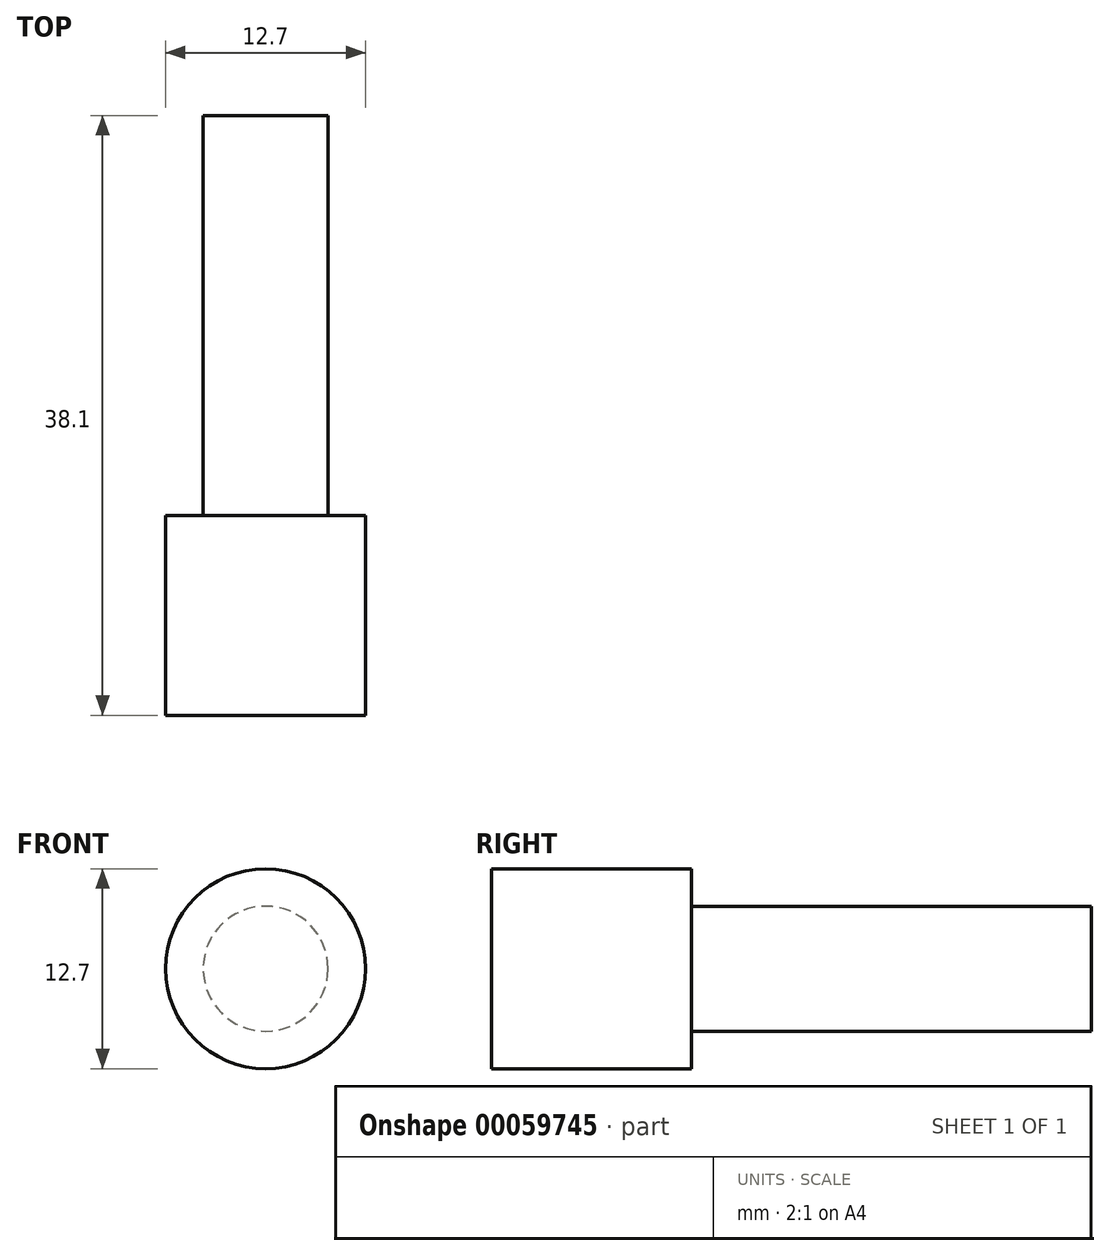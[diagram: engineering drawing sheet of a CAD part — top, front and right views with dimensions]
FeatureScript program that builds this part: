
annotation { "Feature Type Name" : "Feature", "Feature Type Description" : "" }
export const myFeature = defineFeature(function(context is Context, id is Id, definition is map)
    precondition{}
    {
        {
            var Q0;
            Q0=qCreatedBy(makeId("Front.planeOp"),FACE);
            var sketch = newSketch(context, id + "F0", { "sketchPlane" : qUnion([Q0])});
            skCircle(sketch, "E0", {"center": v(0, 0) * mm, "radius": 6.35 * mm});
            skSolve(sketch);
        }
        {
            var Q0;
            Q0=makeQuery(id+"F0.imprint","IMPRINT",FACE,{"disambiguationData":[TD([[makeQuery(id+"F0.imprint","IMPRINT",EDGE,{"derivedFrom":sQuery(id+"F0.wireOp",EDGE,"E0")}),1.0]])]});
            extrude(context, id + "F1", {"entities" : qUnion([Q0]), "depth" : 12.7 * mm});
        }
        {
            var Q0;
            Q0=makeQuery(id+"F1.opExtrude","CAP_FACE",FACE,{"disambiguationData":[OSD([sQuery(id+"F0.wireOp",EDGE,"E0")])],"isStart":true});
            var sketch = newSketch(context, id + "F2", { "sketchPlane" : qUnion([Q0])});
            skCircle(sketch, "E1", {"center": v(0, 0) * mm, "radius": 3.97 * mm});
            skSolve(sketch);
        }
        {
            var Q0;
            Q0=makeQuery(id+"F2.imprint","IMPRINT",FACE,{"disambiguationData":[TD([[makeQuery(id+"F2.imprint","IMPRINT",EDGE,{"derivedFrom":sQuery(id+"F2.wireOp",EDGE,"E1")}),1.0]])]});
            extrude(context, id + "F3", {"entities" : qUnion([Q0]), "operationType" : NewBodyOperationType.ADD, "depth" : 25.4 * mm});
        }
    });
